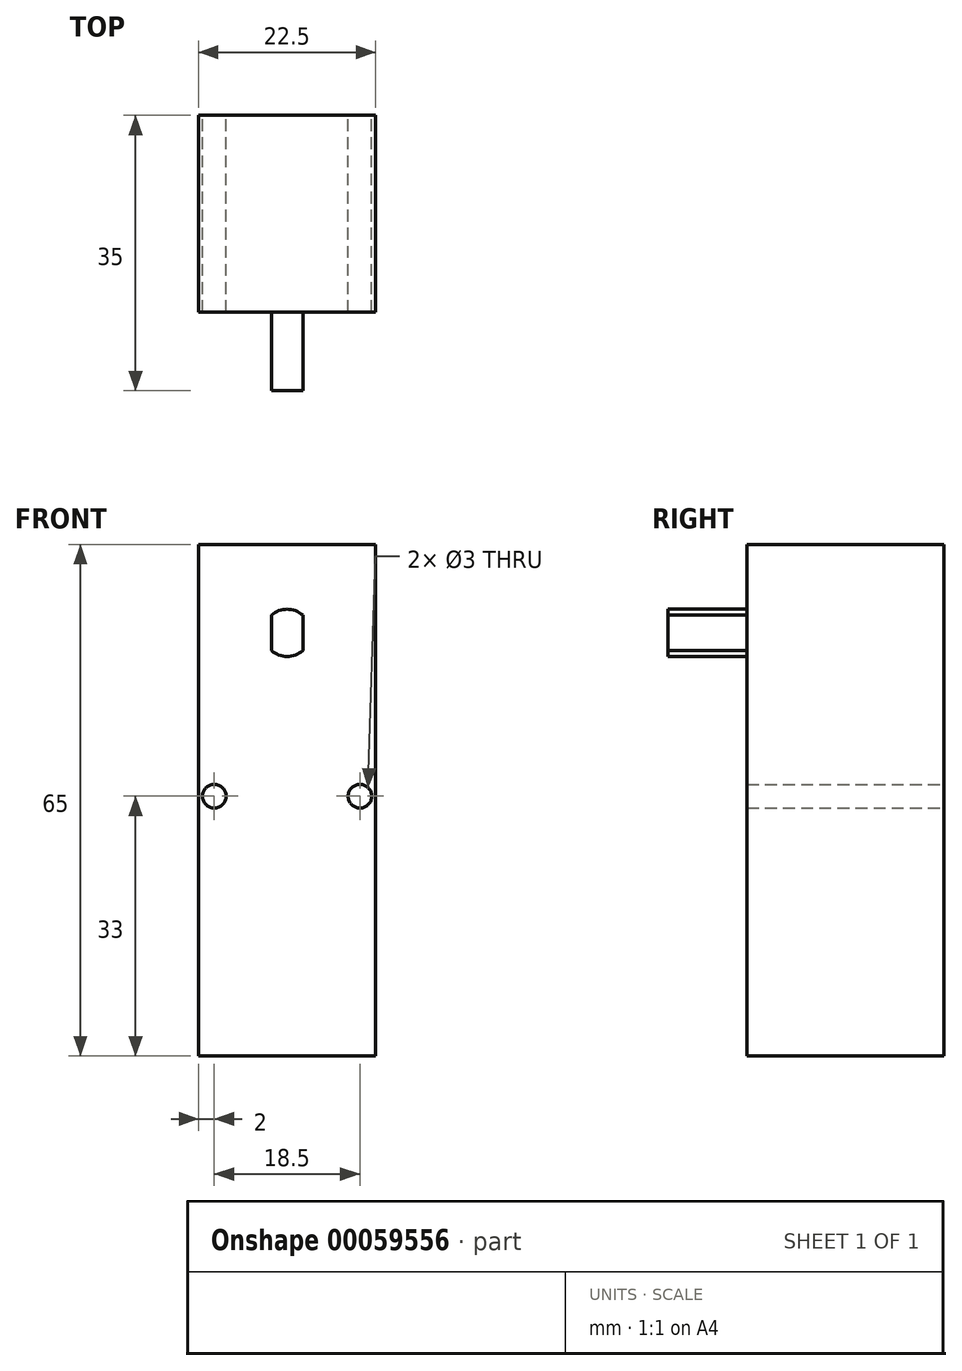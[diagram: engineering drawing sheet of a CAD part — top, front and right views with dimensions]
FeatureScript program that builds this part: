
annotation { "Feature Type Name" : "Feature", "Feature Type Description" : "" }
export const myFeature = defineFeature(function(context is Context, id is Id, definition is map)
    precondition{}
    {
        {
            var Q0;
            Q0=qCreatedBy(makeId("Front.planeOp"),FACE);
            var sketch = newSketch(context, id + "F0", { "sketchPlane" : qUnion([Q0])});
            skLineSegment(sketch, "E0.bottom", {"start": v(-11.25, 32.5) * mm, "end": v(11.25, 32.5) * mm});
            skLineSegment(sketch, "E0.top", {"start": v(-11.25, -32.5) * mm, "end": v(11.25, -32.5) * mm});
            skLineSegment(sketch, "E0.left", {"start": v(-11.25, 32.5) * mm, "end": v(-11.25, -32.5) * mm});
            skLineSegment(sketch, "E0.right", {"start": v(11.25, 32.5) * mm, "end": v(11.25, -32.5) * mm});
            skPoint(sketch, "E0.middle", {"position": v(0, 0) * mm});
            skCircle(sketch, "E1", {"center": v(9.25, 0.5) * mm, "radius": 1.5 * mm});
            skCircle(sketch, "E2.MirrorC", {"center": v(-9.25, 0.5) * mm, "radius": 1.5 * mm});
            skSolve(sketch);
        }
        {
            var Q0;
            Q0 = qSketchRegion(id + "F0", true);
            extrude(context, id + "F1", {"entities" : qUnion([Q0]), "depth" : 25 * mm});
        }
        {
            var Q0;
            Q0=makeQuery(id+"F1.opExtrude","CAP_FACE",FACE,{"disambiguationData":[OSD([sQuery(id+"F0.wireOp",EDGE,"E0.bottom"),sQuery(id+"F0.wireOp",EDGE,"E0.top"),sQuery(id+"F0.wireOp",EDGE,"E0.left"),sQuery(id+"F0.wireOp",EDGE,"E0.right"),sQuery(id+"F0.wireOp",EDGE,"E1"),sQuery(id+"F0.wireOp",EDGE,"E2.MirrorC")])],"isStart":false});
            var sketch = newSketch(context, id + "F2", { "sketchPlane" : qUnion([Q0])});
            skArc(sketch, "E3", {"start": v(2, 23.49) * mm, "mid": v(0, 24.25) * mm, "end": v(-2, 23.49) * mm});
            skLineSegment(sketch, "E4.left", {"start": v(-2, 23.49) * mm, "end": v(-2, 19.01) * mm});
            skLineSegment(sketch, "E4.right", {"start": v(2, 23.49) * mm, "end": v(2, 19.01) * mm});
            skArc(sketch, "E5.trimOffspring", {"start": v(-2, 19.01) * mm, "mid": v(0, 18.25) * mm, "end": v(2, 19.01) * mm});
            skSolve(sketch);
        }
        {
            var Q0;
            Q0 = qSketchRegion(id + "F2", true);
            extrude(context, id + "F3", {"entities" : qUnion([Q0]), "operationType" : NewBodyOperationType.ADD, "depth" : 10 * mm});
        }
    });
